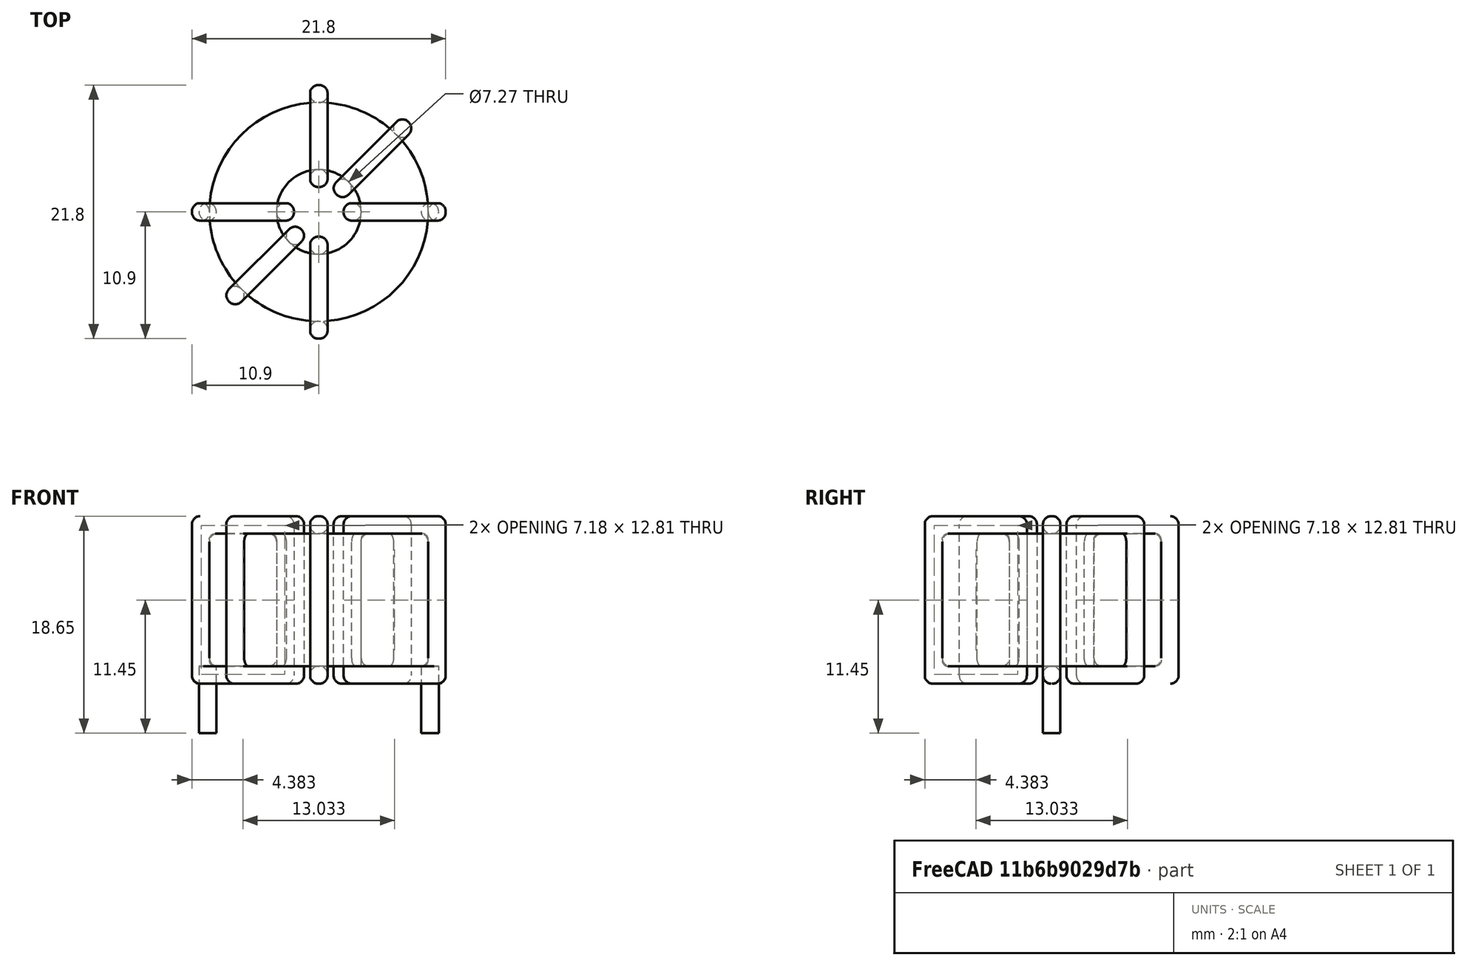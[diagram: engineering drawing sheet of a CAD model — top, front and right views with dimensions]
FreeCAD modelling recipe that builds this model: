
FCSTD DOCUMENT  (FreeCAD 0.16R6703 (Git))
Label: L_Toroid_Horizontal_D21.8mm_P19.10mm_Bourns_2100series
License: All rights reserved
LicenseURL: http://en.wikipedia.org/wiki/All_rights_reserved
objects: Sketcher::SketchObject×6, PartDesign::Pad×6, PartDesign::Fillet×5, Spreadsheet::Sheet×1
note: 23 computed .brp shape members not serialized (recipe doc carries the construction recipe); baked Part::Feature solids carry a one-line shape summary decoded from their .brp

FEATURE [Spreadsheet::Sheet] Spreadsheet  label="dimensions"
  cells = A1=Wx; B1(Wx)=21.8; C1(WW)=7.266666666666667; D1=21.8; A2=Wy; B2(Wy)=21.8; D2=21.8; A3=RM; B3(RMx)=19.1; C3(RMy)=0; A4=d_wire; B4(d_wire)=1.5; A5=H; B5(H)=11.4; A6=offsetx; B6(offsetx)=1.35
FEATURE [Sketcher::SketchObject] Sketch
  Placement = pos=(0,0,2) rot=(0,0,1;0rad)
  expr: Placement.Base.z = 0.5 + Spreadsheet.d_wire
  expr: Constraints[0] = Spreadsheet.Wx / 2 - Spreadsheet.d_wire
  expr: Constraints[4] = Spreadsheet.WW / 2
  expr: Constraints[2] = Spreadsheet.RMy / 2
  expr: Constraints[1] = Spreadsheet.RMx / 2
  sketch-geometry (2):
    g0: Circle CenterX=9.55 CenterY=0 CenterZ=0 NormalX=0 NormalY=0 NormalZ=1 Radius=9.4
    g1: Circle CenterX=9.55 CenterY=0 CenterZ=0 NormalX=0 NormalY=0 NormalZ=1 Radius=3.63333
  constraints (5):
    c: Radius(g0) = 9.4
    c: DistanceX(g-1,g0) = 9.55
    c: DistanceY(g-1,g0) = 0
    c: Coincident(g1,g0)
    c: Radius(g1) = 3.63333
FEATURE [PartDesign::Pad] Pad
  Length = 11.4
  Length2 = 100
  Placement = pos=(0,0,2) rot=(0,0,1;0rad)
  Sketch = -> Sketch
  Type = 0
  expr: Length = Spreadsheet.H
FEATURE [Sketcher::SketchObject] Sketch001
  Placement = pos=(0,0,1.25) rot=(0,0,1;0rad)
  expr: Placement.Base.z = 0.5 + Spreadsheet.d_wire * 0.5
  expr: Constraints[4] = Spreadsheet.RMx
  expr: Constraints[2] = Spreadsheet.RMy
  expr: Constraints[1] = Spreadsheet.d_wire / 2
  sketch-geometry (2):
    g0: Circle CenterX=0 CenterY=0 CenterZ=0 NormalX=0 NormalY=0 NormalZ=1 Radius=0.75
    g1: Circle CenterX=19.1 CenterY=0 CenterZ=0 NormalX=0 NormalY=0 NormalZ=1 Radius=0.75
  constraints (5):
    c: Equal(g0,g1)
    c: Radius(g0) = 0.75
    c: DistanceY(g-1,g1) = 0
    c: Coincident(g0,g-1)
    c: DistanceX(g-1,g1) = 19.1
FEATURE [PartDesign::Pad] Pad001
  Length = 0.75
  Length2 = 5
  Placement = pos=(0,0,1.25) rot=(0,0,1;0rad)
  Reversed = true
  Sketch = -> Sketch001
  Type = 4
  expr: Length2 = 3.5 + Spreadsheet.d_wire
  expr: Length = Spreadsheet.d_wire / 2
FEATURE [PartDesign::Fillet] Fillet
  Base = -> Pad [Edge6,Edge3,Edge2]
  Placement = pos=(0,0,2) rot=(0,0,1;0rad)
  Radius = 0.5
FEATURE [Sketcher::SketchObject] Sketch003
  Placement = pos=(9.55,0,0) rot=(1,0,0;1.5708rad)
  expr: Placement.Base.x = Spreadsheet.RMx / 2
  expr: Constraints[49] = Spreadsheet.Wx - Spreadsheet.d_wire * 2
  expr: Constraints[44] = Spreadsheet.d_wire
  expr: Constraints[23] = Spreadsheet.H
  expr: Constraints[22] = Spreadsheet.Wx / 2 - Spreadsheet.d_wire
  expr: Placement.Base.y = Spreadsheet.RMy / 2
  expr: Constraints[21] = (Spreadsheet.Wx - Spreadsheet.WW) / 2 - Spreadsheet.d_wire
  expr: Constraints[19] = Spreadsheet.d_wire
  expr: Constraints[17] = Spreadsheet.d_wire
  expr: Constraints[18] = Spreadsheet.d_wire
  expr: Constraints[16] = Spreadsheet.d_wire
  sketch-geometry (16):
    g0: LineSegment StartX=-2.13333 StartY=0.5 StartZ=0 EndX=-10.9 EndY=0.5 EndZ=0
    g1: LineSegment StartX=-10.9 StartY=0.5 StartZ=0 EndX=-10.9 EndY=14.9 EndZ=0
    g2: LineSegment StartX=-10.9 StartY=14.9 StartZ=0 EndX=-2.13333 EndY=14.9 EndZ=0
    g3: LineSegment StartX=-2.13333 StartY=14.9 StartZ=0 EndX=-2.13333 EndY=0.5 EndZ=0
    g4: LineSegment StartX=-9.4 StartY=13.4 StartZ=0 EndX=-3.63333 EndY=13.4 EndZ=0
    g5: LineSegment StartX=-3.63333 StartY=13.4 StartZ=0 EndX=-3.63333 EndY=2 EndZ=0
    g6: LineSegment StartX=-3.63333 StartY=2 StartZ=0 EndX=-9.4 EndY=2 EndZ=0
    g7: LineSegment StartX=-9.4 StartY=2 StartZ=0 EndX=-9.4 EndY=13.4 EndZ=0
    g8: LineSegment StartX=2.13333 StartY=14.9 StartZ=0 EndX=10.9 EndY=14.9 EndZ=0
    g9: LineSegment StartX=10.9 StartY=14.9 StartZ=0 EndX=10.9 EndY=0.5 EndZ=0
    g10: LineSegment StartX=10.9 StartY=0.5 StartZ=0 EndX=2.13333 EndY=0.5 EndZ=0
    g11: LineSegment StartX=2.13333 StartY=0.5 StartZ=0 EndX=2.13333 EndY=14.9 EndZ=0
    g12: LineSegment StartX=3.63333 StartY=13.4 StartZ=0 EndX=9.4 EndY=13.4 EndZ=0
    g13: LineSegment StartX=9.4 StartY=13.4 StartZ=0 EndX=9.4 EndY=2 EndZ=0
    g14: LineSegment StartX=9.4 StartY=2 StartZ=0 EndX=3.63333 EndY=2 EndZ=0
    g15: LineSegment StartX=3.63333 StartY=2 StartZ=0 EndX=3.63333 EndY=13.4 EndZ=0
  constraints (50):
    c: Horizontal(g0)
    c: Coincident(g1,g0)
    c: Vertical(g1)
    c: Coincident(g2,g1)
    c: Horizontal(g2)
    c: Coincident(g3,g2)
    c: Coincident(g3,g0)
    c: Vertical(g3)
    c: Coincident(g4,g5)
    c: Coincident(g5,g6)
    c: Coincident(g6,g7)
    c: Coincident(g7,g4)
    c: Horizontal(g4)
    c: Horizontal(g6)
    c: Vertical(g5)
    c: Vertical(g7)
    c: DistanceX(g1,g4) = 1.5
    c: DistanceY(g4,g1) = 1.5
    c: DistanceX(g5,g0) = 1.5
    c: DistanceY(g0,g5) = 1.5
    c: DistanceY(g-1,g0) = 0.5
    c: DistanceX(g6,g6) = 5.76667
    c: DistanceX(g6,g-1) = 9.4
    c: DistanceY(g7,g7) = 11.4
    c: Coincident(g8,g9)
    c: Coincident(g9,g10)
    c: Coincident(g10,g11)
    c: Coincident(g11,g8)
    c: Horizontal(g8)
    c: Horizontal(g10)
    c: Vertical(g9)
    c: Vertical(g11)
    c: Coincident(g12,g13)
    c: Coincident(g13,g14)
    c: Coincident(g14,g15)
    c: Coincident(g15,g12)
    c: Horizontal(g12)
    c: Horizontal(g14)
    c: Vertical(g13)
    c: Vertical(g15)
    c: DistanceY(g8,g2) = 0
    c: DistanceY(g10,g0) = 0
    c: DistanceY(g14,g5) = 0
    c: DistanceY(g12,g4) = 0
    c: DistanceX(g8,g12) = 1.5
    c: Equal(g8,g2)
    c: Equal(g12,g4)
    c: Equal(g9,g1)
    c: Equal(g13,g7)
    c: DistanceX(g4,g12) = 18.8
FEATURE [PartDesign::Pad] Pad002
  Length = 1.5
  Length2 = 100
  Midplane = true
  Placement = pos=(9.55,0,0) rot=(1,0,0;1.5708rad)
  Sketch = -> Sketch003
  Type = 0
  expr: Length = Spreadsheet.d_wire
FEATURE [PartDesign::Fillet] Fillet001
  Base = -> Pad002 [Edge38,Edge41,Edge42,Edge43,Edge29,Edge32,Edge33,Edge34,Edge25,Edge35,Edge36,Edge13,Edge14,Edge15,Edge16,Edge17,Edge18,Edge19,Edge1,Edge2,Edge3,Edge4,Edge5,Edge6,Edge7,Edge37,Edge39,Edge40,Edge20,Edge23,Edge24,Edge21,Edge22,Edge8,Edge9,Edge10,Edge11,Edge12,Edge26,Edge27,+8 more]
  Placement = pos=(9.55,0,0) rot=(1,0,0;1.5708rad)
  Radius = 0.705
  expr: Radius = Spreadsheet.d_wire * 0.47
FEATURE [Sketcher::SketchObject] Sketch004
  Placement = pos=(9.55,0,0) rot=(0.862856,0.357407,0.357407;1.71777rad)
  expr: Placement.Base.x = Spreadsheet.RMx / 2
  expr: Constraints[49] = Spreadsheet.Wx - 2 * Spreadsheet.d_wire
  expr: Constraints[44] = Spreadsheet.d_wire
  expr: Constraints[23] = Spreadsheet.H
  expr: Constraints[22] = Spreadsheet.Wx / 2 - Spreadsheet.d_wire
  expr: Placement.Base.y = Spreadsheet.RMy / 2
  expr: Constraints[21] = (Spreadsheet.Wx - Spreadsheet.WW) / 2 - Spreadsheet.d_wire
  expr: Constraints[19] = Spreadsheet.d_wire
  expr: Constraints[17] = Spreadsheet.d_wire
  expr: Constraints[18] = Spreadsheet.d_wire
  expr: Constraints[16] = Spreadsheet.d_wire
  sketch-geometry (16):
    g0: LineSegment StartX=-2.13333 StartY=0.5 StartZ=0 EndX=-10.9 EndY=0.5 EndZ=0
    g1: LineSegment StartX=-10.9 StartY=0.5 StartZ=0 EndX=-10.9 EndY=14.9 EndZ=0
    g2: LineSegment StartX=-10.9 StartY=14.9 StartZ=0 EndX=-2.13333 EndY=14.9 EndZ=0
    g3: LineSegment StartX=-2.13333 StartY=14.9 StartZ=0 EndX=-2.13333 EndY=0.5 EndZ=0
    g4: LineSegment StartX=-9.4 StartY=13.4 StartZ=0 EndX=-3.63333 EndY=13.4 EndZ=0
    g5: LineSegment StartX=-3.63333 StartY=13.4 StartZ=0 EndX=-3.63333 EndY=2 EndZ=0
    g6: LineSegment StartX=-3.63333 StartY=2 StartZ=0 EndX=-9.4 EndY=2 EndZ=0
    g7: LineSegment StartX=-9.4 StartY=2 StartZ=0 EndX=-9.4 EndY=13.4 EndZ=0
    g8: LineSegment StartX=2.13333 StartY=14.9 StartZ=0 EndX=10.9 EndY=14.9 EndZ=0
    g9: LineSegment StartX=10.9 StartY=14.9 StartZ=0 EndX=10.9 EndY=0.5 EndZ=0
    g10: LineSegment StartX=10.9 StartY=0.5 StartZ=0 EndX=2.13333 EndY=0.5 EndZ=0
    g11: LineSegment StartX=2.13333 StartY=0.5 StartZ=0 EndX=2.13333 EndY=14.9 EndZ=0
    g12: LineSegment StartX=3.63333 StartY=13.4 StartZ=0 EndX=9.4 EndY=13.4 EndZ=0
    g13: LineSegment StartX=9.4 StartY=13.4 StartZ=0 EndX=9.4 EndY=2 EndZ=0
    g14: LineSegment StartX=9.4 StartY=2 StartZ=0 EndX=3.63333 EndY=2 EndZ=0
    g15: LineSegment StartX=3.63333 StartY=2 StartZ=0 EndX=3.63333 EndY=13.4 EndZ=0
  constraints (50):
    c: Horizontal(g0)
    c: Coincident(g1,g0)
    c: Vertical(g1)
    c: Coincident(g2,g1)
    c: Horizontal(g2)
    c: Coincident(g3,g2)
    c: Coincident(g3,g0)
    c: Vertical(g3)
    c: Coincident(g4,g5)
    c: Coincident(g5,g6)
    c: Coincident(g6,g7)
    c: Coincident(g7,g4)
    c: Horizontal(g4)
    c: Horizontal(g6)
    c: Vertical(g5)
    c: Vertical(g7)
    c: DistanceX(g1,g4) = 1.5
    c: DistanceY(g4,g1) = 1.5
    c: DistanceX(g5,g0) = 1.5
    c: DistanceY(g0,g5) = 1.5
    c: DistanceY(g-1,g0) = 0.5
    c: DistanceX(g6,g6) = 5.76667
    c: DistanceX(g6,g-1) = 9.4
    c: DistanceY(g7,g7) = 11.4
    c: Coincident(g8,g9)
    c: Coincident(g9,g10)
    c: Coincident(g10,g11)
    c: Coincident(g11,g8)
    c: Horizontal(g8)
    c: Horizontal(g10)
    c: Vertical(g9)
    c: Vertical(g11)
    c: Coincident(g12,g13)
    c: Coincident(g13,g14)
    c: Coincident(g14,g15)
    c: Coincident(g15,g12)
    c: Horizontal(g12)
    c: Horizontal(g14)
    c: Vertical(g13)
    c: Vertical(g15)
    c: DistanceY(g8,g2) = 0
    c: DistanceY(g10,g0) = 0
    c: DistanceY(g14,g5) = 0
    c: DistanceY(g12,g4) = 0
    c: DistanceX(g8,g12) = 1.5
    c: Equal(g8,g2)
    c: Equal(g12,g4)
    c: Equal(g9,g1)
    c: Equal(g13,g7)
    c: DistanceX(g4,g12) = 18.8
FEATURE [PartDesign::Pad] Pad003
  Length = 1.5
  Length2 = 100
  Midplane = true
  Placement = pos=(9.55,0,0) rot=(0.862856,0.357407,0.357407;1.71777rad)
  Sketch = -> Sketch004
  Type = 0
  expr: Length = Spreadsheet.d_wire
FEATURE [PartDesign::Fillet] Fillet002
  Base = -> Pad003 [Edge38,Edge41,Edge42,Edge43,Edge29,Edge32,Edge33,Edge34,Edge25,Edge35,Edge36,Edge13,Edge14,Edge15,Edge16,Edge17,Edge18,Edge19,Edge1,Edge2,Edge3,Edge4,Edge5,Edge6,Edge7,Edge37,Edge39,Edge40,Edge20,Edge23,Edge24,Edge21,Edge22,Edge8,Edge9,Edge10,Edge11,Edge12,Edge26,Edge27,+8 more]
  Placement = pos=(9.55,0,0) rot=(0.862856,0.357407,0.357407;1.71777rad)
  Radius = 0.705
  expr: Radius = Spreadsheet.d_wire * 0.47
FEATURE [Sketcher::SketchObject] Sketch005
  Placement = pos=(9.55,0,0) rot=(0.862856,-0.357407,-0.357407;1.71777rad)
  expr: Placement.Base.x = Spreadsheet.RMx / 2
  expr: Constraints[49] = Spreadsheet.Wx - 2 * Spreadsheet.d_wire
  expr: Constraints[44] = Spreadsheet.d_wire
  expr: Constraints[23] = Spreadsheet.H
  expr: Constraints[22] = Spreadsheet.Wx / 2 - Spreadsheet.d_wire
  expr: Placement.Base.y = Spreadsheet.RMy / 2
  expr: Constraints[21] = (Spreadsheet.Wx - Spreadsheet.WW) / 2 - Spreadsheet.d_wire
  expr: Constraints[19] = Spreadsheet.d_wire
  expr: Constraints[17] = Spreadsheet.d_wire
  expr: Constraints[18] = Spreadsheet.d_wire
  expr: Constraints[16] = Spreadsheet.d_wire
  sketch-geometry (16):
    g0: LineSegment StartX=-2.13333 StartY=0.5 StartZ=0 EndX=-10.9 EndY=0.5 EndZ=0
    g1: LineSegment StartX=-10.9 StartY=0.5 StartZ=0 EndX=-10.9 EndY=14.9 EndZ=0
    g2: LineSegment StartX=-10.9 StartY=14.9 StartZ=0 EndX=-2.13333 EndY=14.9 EndZ=0
    g3: LineSegment StartX=-2.13333 StartY=14.9 StartZ=0 EndX=-2.13333 EndY=0.5 EndZ=0
    g4: LineSegment StartX=-9.4 StartY=13.4 StartZ=0 EndX=-3.63333 EndY=13.4 EndZ=0
    g5: LineSegment StartX=-3.63333 StartY=13.4 StartZ=0 EndX=-3.63333 EndY=2 EndZ=0
    g6: LineSegment StartX=-3.63333 StartY=2 StartZ=0 EndX=-9.4 EndY=2 EndZ=0
    g7: LineSegment StartX=-9.4 StartY=2 StartZ=0 EndX=-9.4 EndY=13.4 EndZ=0
    g8: LineSegment StartX=2.13333 StartY=14.9 StartZ=0 EndX=10.9 EndY=14.9 EndZ=0
    g9: LineSegment StartX=10.9 StartY=14.9 StartZ=0 EndX=10.9 EndY=0.5 EndZ=0
    g10: LineSegment StartX=10.9 StartY=0.5 StartZ=0 EndX=2.13333 EndY=0.5 EndZ=0
    g11: LineSegment StartX=2.13333 StartY=0.5 StartZ=0 EndX=2.13333 EndY=14.9 EndZ=0
    g12: LineSegment StartX=3.63333 StartY=13.4 StartZ=0 EndX=9.4 EndY=13.4 EndZ=0
    g13: LineSegment StartX=9.4 StartY=13.4 StartZ=0 EndX=9.4 EndY=2 EndZ=0
    g14: LineSegment StartX=9.4 StartY=2 StartZ=0 EndX=3.63333 EndY=2 EndZ=0
    g15: LineSegment StartX=3.63333 StartY=2 StartZ=0 EndX=3.63333 EndY=13.4 EndZ=0
  constraints (50):
    c: Horizontal(g0)
    c: Coincident(g1,g0)
    c: Vertical(g1)
    c: Coincident(g2,g1)
    c: Horizontal(g2)
    c: Coincident(g3,g2)
    c: Coincident(g3,g0)
    c: Vertical(g3)
    c: Coincident(g4,g5)
    c: Coincident(g5,g6)
    c: Coincident(g6,g7)
    c: Coincident(g7,g4)
    c: Horizontal(g4)
    c: Horizontal(g6)
    c: Vertical(g5)
    c: Vertical(g7)
    c: DistanceX(g1,g4) = 1.5
    c: DistanceY(g4,g1) = 1.5
    c: DistanceX(g5,g0) = 1.5
    c: DistanceY(g0,g5) = 1.5
    c: DistanceY(g-1,g0) = 0.5
    c: DistanceX(g6,g6) = 5.76667
    c: DistanceX(g6,g-1) = 9.4
    c: DistanceY(g7,g7) = 11.4
    c: Coincident(g8,g9)
    c: Coincident(g9,g10)
    c: Coincident(g10,g11)
    c: Coincident(g11,g8)
    c: Horizontal(g8)
    c: Horizontal(g10)
    c: Vertical(g9)
    c: Vertical(g11)
    c: Coincident(g12,g13)
    c: Coincident(g13,g14)
    c: Coincident(g14,g15)
    c: Coincident(g15,g12)
    c: Horizontal(g12)
    c: Horizontal(g14)
    c: Vertical(g13)
    c: Vertical(g15)
    c: DistanceY(g8,g2) = 0
    c: DistanceY(g10,g0) = 0
    c: DistanceY(g14,g5) = 0
    c: DistanceY(g12,g4) = 0
    c: DistanceX(g8,g12) = 1.5
    c: Equal(g8,g2)
    c: Equal(g12,g4)
    c: Equal(g9,g1)
    c: Equal(g13,g7)
    c: DistanceX(g4,g12) = 18.8
FEATURE [PartDesign::Pad] Pad004
  Length = 1.5
  Length2 = 100
  Midplane = true
  Placement = pos=(9.55,0,0) rot=(0.862856,-0.357407,-0.357407;1.71777rad)
  Sketch = -> Sketch005
  Type = 0
  expr: Length = Spreadsheet.d_wire
FEATURE [PartDesign::Fillet] Fillet003
  Base = -> Pad004 [Edge38,Edge41,Edge42,Edge43,Edge29,Edge32,Edge33,Edge34,Edge25,Edge35,Edge36,Edge13,Edge14,Edge15,Edge16,Edge17,Edge18,Edge19,Edge1,Edge2,Edge3,Edge4,Edge5,Edge6,Edge7,Edge37,Edge39,Edge40,Edge20,Edge23,Edge24,Edge21,Edge22,Edge8,Edge9,Edge10,Edge11,Edge12,Edge26,Edge27,+8 more]
  Placement = pos=(9.55,0,0) rot=(0.862856,-0.357407,-0.357407;1.71777rad)
  Radius = 0.705
  expr: Radius = Spreadsheet.d_wire * 0.47
FEATURE [Sketcher::SketchObject] Sketch006
  Placement = pos=(9.55,0,0) rot=(0.57735,0.57735,0.57735;2.0944rad)
  expr: Placement.Base.x = Spreadsheet.RMx / 2
  expr: Constraints[49] = Spreadsheet.Wx - Spreadsheet.d_wire * 2
  expr: Constraints[44] = Spreadsheet.d_wire
  expr: Constraints[23] = Spreadsheet.H
  expr: Constraints[22] = Spreadsheet.Wx / 2 - Spreadsheet.d_wire
  expr: Placement.Base.y = Spreadsheet.RMy / 2
  expr: Constraints[21] = (Spreadsheet.Wx - Spreadsheet.WW) / 2 - Spreadsheet.d_wire
  expr: Constraints[19] = Spreadsheet.d_wire
  expr: Constraints[17] = Spreadsheet.d_wire
  expr: Constraints[18] = Spreadsheet.d_wire
  expr: Constraints[16] = Spreadsheet.d_wire
  sketch-geometry (16):
    g0: LineSegment StartX=-2.13333 StartY=0.5 StartZ=0 EndX=-10.9 EndY=0.5 EndZ=0
    g1: LineSegment StartX=-10.9 StartY=0.5 StartZ=0 EndX=-10.9 EndY=14.9 EndZ=0
    g2: LineSegment StartX=-10.9 StartY=14.9 StartZ=0 EndX=-2.13333 EndY=14.9 EndZ=0
    g3: LineSegment StartX=-2.13333 StartY=14.9 StartZ=0 EndX=-2.13333 EndY=0.5 EndZ=0
    g4: LineSegment StartX=-9.4 StartY=13.4 StartZ=0 EndX=-3.63333 EndY=13.4 EndZ=0
    g5: LineSegment StartX=-3.63333 StartY=13.4 StartZ=0 EndX=-3.63333 EndY=2 EndZ=0
    g6: LineSegment StartX=-3.63333 StartY=2 StartZ=0 EndX=-9.4 EndY=2 EndZ=0
    g7: LineSegment StartX=-9.4 StartY=2 StartZ=0 EndX=-9.4 EndY=13.4 EndZ=0
    g8: LineSegment StartX=2.13333 StartY=14.9 StartZ=0 EndX=10.9 EndY=14.9 EndZ=0
    g9: LineSegment StartX=10.9 StartY=14.9 StartZ=0 EndX=10.9 EndY=0.5 EndZ=0
    g10: LineSegment StartX=10.9 StartY=0.5 StartZ=0 EndX=2.13333 EndY=0.5 EndZ=0
    g11: LineSegment StartX=2.13333 StartY=0.5 StartZ=0 EndX=2.13333 EndY=14.9 EndZ=0
    g12: LineSegment StartX=3.63333 StartY=13.4 StartZ=0 EndX=9.4 EndY=13.4 EndZ=0
    g13: LineSegment StartX=9.4 StartY=13.4 StartZ=0 EndX=9.4 EndY=2 EndZ=0
    g14: LineSegment StartX=9.4 StartY=2 StartZ=0 EndX=3.63333 EndY=2 EndZ=0
    g15: LineSegment StartX=3.63333 StartY=2 StartZ=0 EndX=3.63333 EndY=13.4 EndZ=0
  constraints (50):
    c: Horizontal(g0)
    c: Coincident(g1,g0)
    c: Vertical(g1)
    c: Coincident(g2,g1)
    c: Horizontal(g2)
    c: Coincident(g3,g2)
    c: Coincident(g3,g0)
    c: Vertical(g3)
    c: Coincident(g4,g5)
    c: Coincident(g5,g6)
    c: Coincident(g6,g7)
    c: Coincident(g7,g4)
    c: Horizontal(g4)
    c: Horizontal(g6)
    c: Vertical(g5)
    c: Vertical(g7)
    c: DistanceX(g1,g4) = 1.5
    c: DistanceY(g4,g1) = 1.5
    c: DistanceX(g5,g0) = 1.5
    c: DistanceY(g0,g5) = 1.5
    c: DistanceY(g-1,g0) = 0.5
    c: DistanceX(g6,g6) = 5.76667
    c: DistanceX(g6,g-1) = 9.4
    c: DistanceY(g7,g7) = 11.4
    c: Coincident(g8,g9)
    c: Coincident(g9,g10)
    c: Coincident(g10,g11)
    c: Coincident(g11,g8)
    c: Horizontal(g8)
    c: Horizontal(g10)
    c: Vertical(g9)
    c: Vertical(g11)
    c: Coincident(g12,g13)
    c: Coincident(g13,g14)
    c: Coincident(g14,g15)
    c: Coincident(g15,g12)
    c: Horizontal(g12)
    c: Horizontal(g14)
    c: Vertical(g13)
    c: Vertical(g15)
    c: DistanceY(g8,g2) = 0
    c: DistanceY(g10,g0) = 0
    c: DistanceY(g14,g5) = 0
    c: DistanceY(g12,g4) = 0
    c: DistanceX(g8,g12) = 1.5
    c: Equal(g8,g2)
    c: Equal(g12,g4)
    c: Equal(g9,g1)
    c: Equal(g13,g7)
    c: DistanceX(g4,g12) = 18.8
FEATURE [PartDesign::Pad] Pad005
  Length = 1.5
  Length2 = 100
  Midplane = true
  Placement = pos=(9.55,0,0) rot=(0.57735,0.57735,0.57735;2.0944rad)
  Sketch = -> Sketch006
  Type = 0
  expr: Length = Spreadsheet.d_wire
FEATURE [PartDesign::Fillet] Fillet004
  Base = -> Pad005 [Edge38,Edge41,Edge42,Edge43,Edge29,Edge32,Edge33,Edge34,Edge25,Edge35,Edge36,Edge13,Edge14,Edge15,Edge16,Edge17,Edge18,Edge19,Edge1,Edge2,Edge3,Edge4,Edge5,Edge6,Edge7,Edge37,Edge39,Edge40,Edge20,Edge23,Edge24,Edge21,Edge22,Edge8,Edge9,Edge10,Edge11,Edge12,Edge26,Edge27,+8 more]
  Placement = pos=(9.55,0,0) rot=(0.57735,0.57735,0.57735;2.0944rad)
  Radius = 0.705
  expr: Radius = Spreadsheet.d_wire * 0.47
